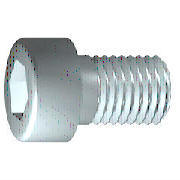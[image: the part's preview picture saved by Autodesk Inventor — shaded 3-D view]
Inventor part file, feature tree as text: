
AUTODESK INVENTOR PART (.ipt)
format: ipt  version: 2022 (Build 260153000, 153)  size: 191,488 bytes
history: native  units: mm (DEFAULTED — no unit token found)
features: sketch x2, other x1, extrude x1, plane x1, fillet x1
ambient origin geometry x7: Origin, YZ Plane, XY Plane, X Axis, Y Axis, Z Axis, Center Point
bodies: Solid1 (feature_tree)
feature tree (6):
  other  "Cuerpo"
  extrude  "Ranura"  Depth=1.6mm
  plane  "Work Plane1"
  fillet  "Fillet2"  Radius=1.6mm
  sketch  "Boceto1"  dims[d1=9.125mm d2=0.214807mm d3=1.6mm]
  sketch  "Boceto2"  dims[d4=0.7mm d5=60.0deg d6=1.6mm d7=1.6mm d8=1.732051mm d9=3.0mm d10=90.0deg d11=10.0mm d12=0.0mm d13=9.125mm d14=0.0mm d15=0.214707mm d16=0.214707mm d17=0.16mm d19=0.0mm d26=10.0mm d27=45.0deg d28=0.0mm d29=0.0mm d30=0.1mm]
